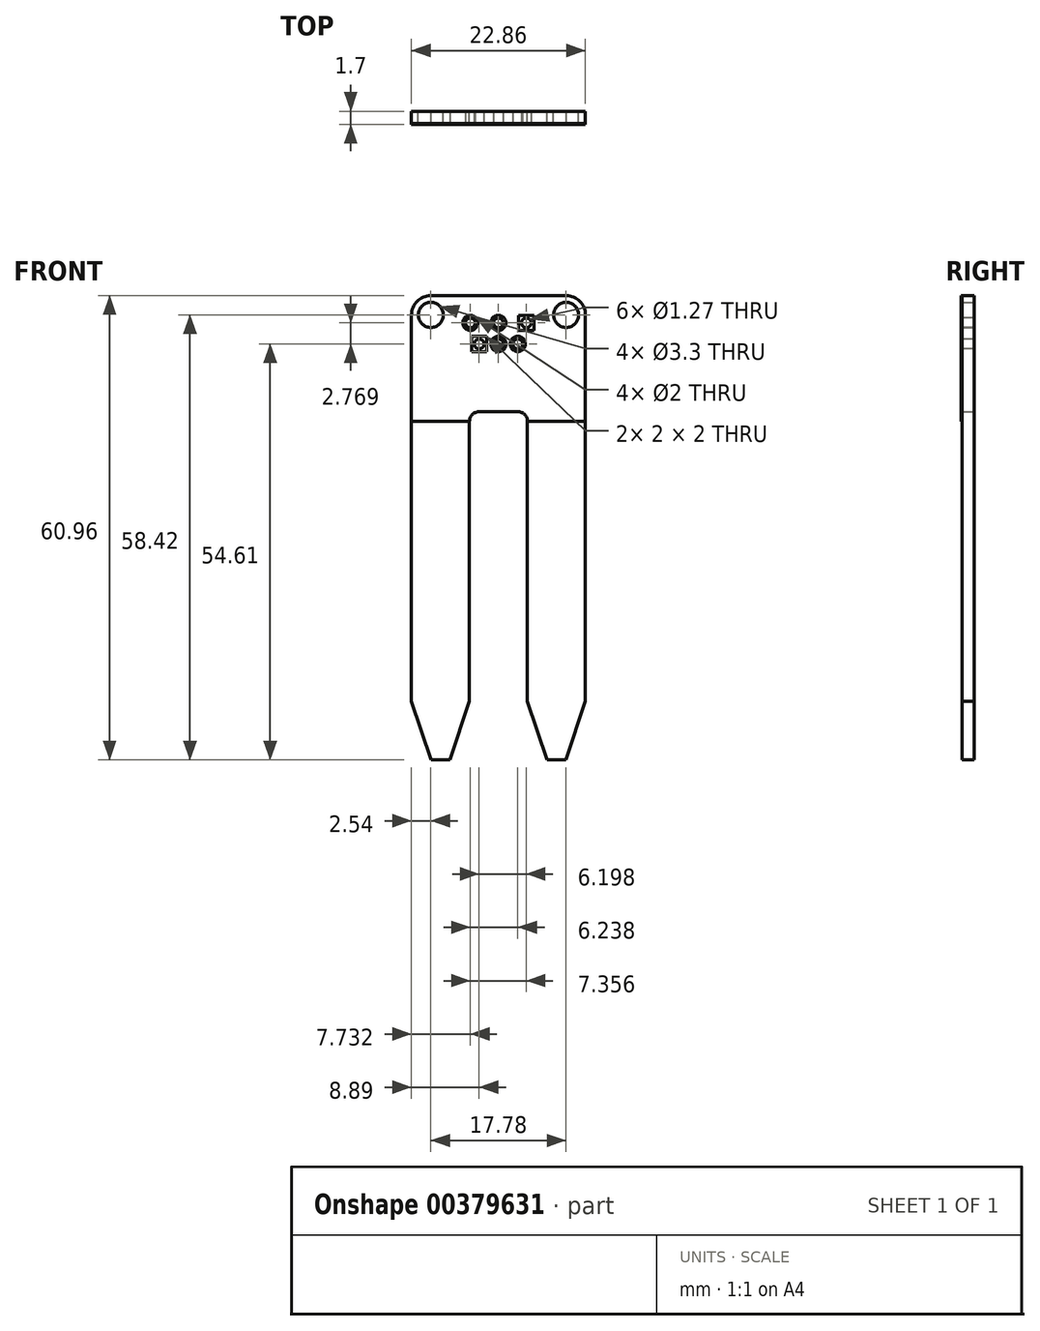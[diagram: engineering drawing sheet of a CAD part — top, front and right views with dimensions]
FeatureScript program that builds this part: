
annotation { "Feature Type Name" : "Feature", "Feature Type Description" : "" }
export const myFeature = defineFeature(function(context is Context, id is Id, definition is map)
    precondition{}
    {
        {
            var Q0;
            Q0=qCreatedBy(makeId("Front.planeOp"),FACE);
            var sketch = newSketch(context, id + "F0", { "sketchPlane" : qUnion([Q0])});
            skLineSegment(sketch, "E0.bottom", {"start": v(0, 0) * mm, "end": v(22.86, 0) * mm});
            skLineSegment(sketch, "E0.top", {"start": v(0, -15.24) * mm, "end": v(22.86, -15.24) * mm});
            skLineSegment(sketch, "E0.left", {"start": v(0, 0) * mm, "end": v(0, -15.24) * mm});
            skLineSegment(sketch, "E0.right", {"start": v(22.86, 0) * mm, "end": v(22.86, -15.24) * mm});
            skLineSegment(sketch, "E1.bottom", {"start": v(0, -15.24) * mm, "end": v(7.62, -15.24) * mm});
            skLineSegment(sketch, "E1.top", {"start": v(0, -60.96) * mm, "end": v(7.62, -60.96) * mm});
            skLineSegment(sketch, "E1.left", {"start": v(0, -15.24) * mm, "end": v(0, -60.96) * mm});
            skLineSegment(sketch, "E1.right", {"start": v(7.62, -15.24) * mm, "end": v(7.62, -60.96) * mm});
            skLineSegment(sketch, "E2.bottom", {"start": v(22.86, -15.24) * mm, "end": v(15.24, -15.24) * mm});
            skLineSegment(sketch, "E2.top", {"start": v(22.86, -60.96) * mm, "end": v(15.24, -60.96) * mm});
            skLineSegment(sketch, "E2.left", {"start": v(22.86, -15.24) * mm, "end": v(22.86, -60.96) * mm});
            skLineSegment(sketch, "E2.right", {"start": v(15.24, -15.24) * mm, "end": v(15.24, -60.96) * mm});
            skCircle(sketch, "E3", {"center": v(2.54, -2.54) * mm, "radius": 1.65 * mm});
            skCircle(sketch, "E4", {"center": v(20.32, -2.54) * mm, "radius": 1.65 * mm});
            skSolve(sketch);
        }
        {
            var Q0;
            Q0=qSketchRegion(id+"F0",true);
            extrude(context, id + "F1", {"entities" : qUnion([Q0]), "depth" : 1.6 * mm});
        }
        {
            var Q0;
            Q0=makeQuery(id+"F1.opExtrude","SWEPT_EDGE",EDGE,{"disambiguationData":[OSD([sQuery(id+"F0.wireOp",EDGE,"E0.bottom"),sQuery(id+"F0.wireOp",EDGE,"E0.left")])]});
            var Q1;
            Q1=makeQuery(id+"F1.opExtrude","SWEPT_EDGE",EDGE,{"disambiguationData":[OSD([sQuery(id+"F0.wireOp",EDGE,"E0.bottom"),sQuery(id+"F0.wireOp",EDGE,"E0.right")])]});
            fillet(context, id + "F2", {"entities" : qUnion([Q0, Q1]), "radius" : 2.54 * mm, "tangentPropagation" : true, "allowEdgeOverflow" : false});
        }
        {
            var Q0;
            Q0=makeQuery(id+"F1.opExtrude","SWEPT_EDGE",EDGE,{"disambiguationData":[OSD([sQuery(id+"F0.wireOp",EDGE,"E1.top"),sQuery(id+"F0.wireOp",EDGE,"E1.left")])]});
            var Q1;
            Q1=makeQuery(id+"F1.opExtrude","SWEPT_EDGE",EDGE,{"disambiguationData":[OSD([sQuery(id+"F0.wireOp",EDGE,"E1.top"),sQuery(id+"F0.wireOp",EDGE,"E1.right")])]});
            var Q2;
            Q2=makeQuery(id+"F1.opExtrude","SWEPT_EDGE",EDGE,{"disambiguationData":[OSD([sQuery(id+"F0.wireOp",EDGE,"E2.top"),sQuery(id+"F0.wireOp",EDGE,"E2.right")])]});
            chamfer(context, id + "F3", {"entities" : qUnion([Q0, Q1, Q2]), "chamferType" : ChamferType.TWO_OFFSETS, "width1" : 2.59 * mm, "oppositeDirection" : false, "width2" : 7.66 * mm, "tangentPropagation" : true});
        }
        {
            var Q0;
            Q0=makeQuery(id+"F1.opExtrude","SWEPT_EDGE",EDGE,{"disambiguationData":[OSD([sQuery(id+"F0.wireOp",EDGE,"E2.top"),sQuery(id+"F0.wireOp",EDGE,"E2.left")])]});
            chamfer(context, id + "F4", {"entities" : qUnion([Q0]), "chamferType" : ChamferType.TWO_OFFSETS, "width1" : 7.66 * mm, "oppositeDirection" : false, "width2" : 2.59 * mm, "tangentPropagation" : true});
        }
        {
            var Q0;
            Q0=makeQuery(id+"F1.opExtrude","SWEPT_EDGE",EDGE,{"disambiguationData":[OSD([sQuery(id+"F0.wireOp",EDGE,"E0.top"),sQuery(id+"F0.wireOp",EDGE,"E1.bottom"),sQuery(id+"F0.wireOp",EDGE,"E1.right")])]});
            var Q1;
            Q1=makeQuery(id+"F1.opExtrude","SWEPT_EDGE",EDGE,{"disambiguationData":[OSD([sQuery(id+"F0.wireOp",EDGE,"E0.top"),sQuery(id+"F0.wireOp",EDGE,"E2.bottom"),sQuery(id+"F0.wireOp",EDGE,"E2.right")])]});
            fillet(context, id + "F5", {"entities" : qUnion([Q0, Q1]), "radius" : 1.27 * mm, "tangentPropagation" : true, "allowEdgeOverflow" : false});
        }
        {
            var Q0;
            Q0=makeQuery(id+"F1.opExtrude","CAP_FACE",FACE,{"disambiguationData":[OSD([sQuery(id+"F0.wireOp",EDGE,"E0.bottom"),sQuery(id+"F0.wireOp",EDGE,"E0.top"),sQuery(id+"F0.wireOp",EDGE,"E0.left"),sQuery(id+"F0.wireOp",EDGE,"E0.right"),sQuery(id+"F0.wireOp",EDGE,"E1.top"),sQuery(id+"F0.wireOp",EDGE,"E1.left"),sQuery(id+"F0.wireOp",EDGE,"E1.right"),sQuery(id+"F0.wireOp",EDGE,"E2.top"),sQuery(id+"F0.wireOp",EDGE,"E2.left"),sQuery(id+"F0.wireOp",EDGE,"E2.right"),sQuery(id+"F0.wireOp",EDGE,"E3"),sQuery(id+"F0.wireOp",EDGE,"E4")])],"isStart":false});
            var sketch = newSketch(context, id + "F6", { "sketchPlane" : qUnion([Q0])});
            skCircle(sketch, "E5", {"center": v(7.73, -3.58) * mm, "radius": 0.64 * mm});
            skCircle(sketch, "E6.1.0.0", {"center": v(11.4, -3.58) * mm, "radius": 0.64 * mm});
            skCircle(sketch, "E6.2.0.0", {"center": v(15.09, -3.58) * mm, "radius": 0.64 * mm});
            skLineSegment(sketch, "E6.direction1", {"start": v(7.73, -3.58) * mm, "end": v(11.4, -3.58) * mm, "construction": true});
            skCircle(sketch, "E7", {"center": v(8.9, -6.35) * mm, "radius": 0.64 * mm});
            skCircle(sketch, "E8.1.0.0", {"center": v(11.43, -6.35) * mm, "radius": 0.64 * mm});
            skCircle(sketch, "E8.2.0.0", {"center": v(13.97, -6.35) * mm, "radius": 0.64 * mm});
            skLineSegment(sketch, "E8.direction1", {"start": v(8.9, -6.35) * mm, "end": v(11.43, -6.35) * mm, "construction": true});
            skSolve(sketch);
        }
        {
            var Q0;
            Q0=qSketchRegion(id+"F6",true);
            extrude(context, id + "F7", {"entities" : qUnion([Q0]), "operationType" : NewBodyOperationType.REMOVE, "endBound" : BoundingType.THROUGH_ALL, "oppositeDirection" : true, "depth" : 25 * mm});
        }
        {
            var Q0;
            Q0=makeQuery(id+"F1.opExtrude","CAP_FACE",FACE,{"disambiguationData":[OSD([sQuery(id+"F0.wireOp",EDGE,"E0.bottom"),sQuery(id+"F0.wireOp",EDGE,"E0.top"),sQuery(id+"F0.wireOp",EDGE,"E0.left"),sQuery(id+"F0.wireOp",EDGE,"E0.right"),sQuery(id+"F0.wireOp",EDGE,"E1.top"),sQuery(id+"F0.wireOp",EDGE,"E1.left"),sQuery(id+"F0.wireOp",EDGE,"E1.right"),sQuery(id+"F0.wireOp",EDGE,"E2.top"),sQuery(id+"F0.wireOp",EDGE,"E2.left"),sQuery(id+"F0.wireOp",EDGE,"E2.right"),sQuery(id+"F0.wireOp",EDGE,"E3"),sQuery(id+"F0.wireOp",EDGE,"E4")])],"isStart":false});
            var sketch = newSketch(context, id + "F8", { "sketchPlane" : qUnion([Q0])});
            skCircle(sketch, "E9", {"center": v(2.54, -2.54) * mm, "radius": 1.65 * mm});
            skCircle(sketch, "E10", {"center": v(20.32, -2.54) * mm, "radius": 1.65 * mm});
            skCircle(sketch, "E11", {"center": v(7.73, -3.58) * mm, "radius": 1 * mm});
            skCircle(sketch, "E12", {"center": v(11.4, -3.58) * mm, "radius": 1 * mm});
            skCircle(sketch, "E13", {"center": v(11.43, -6.35) * mm, "radius": 1 * mm});
            skCircle(sketch, "E14", {"center": v(13.97, -6.35) * mm, "radius": 1 * mm});
            skLineSegment(sketch, "E15", {"start": v(0, -16.5) * mm, "end": v(22.86, -16.5) * mm});
            skLineSegment(sketch, "E16", {"start": v(22.86, -16.5) * mm, "end": v(22.86, -2.54) * mm});
            skLineSegment(sketch, "E17", {"start": v(20.32, 0) * mm, "end": v(2.54, 0) * mm});
            skLineSegment(sketch, "E18", {"start": v(0, -2.54) * mm, "end": v(0, -16.5) * mm});
            skPoint(sketch, "E19.visualSharp", {"position": v(0, 0) * mm});
            skArc(sketch, "E19.filletArc", {"start": v(2.54, 0) * mm, "mid": v(0.74, -0.74) * mm, "end": v(0, -2.54) * mm});
            skPoint(sketch, "E20.visualSharp", {"position": v(22.86, 0) * mm});
            skArc(sketch, "E20.filletArc", {"start": v(22.86, -2.54) * mm, "mid": v(22.12, -0.74) * mm, "end": v(20.32, 0) * mm});
            skLineSegment(sketch, "E21", {"start": v(7.62, -16.5) * mm, "end": v(7.62, -16.5) * mm});
            skLineSegment(sketch, "E22", {"start": v(8.9, -15.24) * mm, "end": v(13.97, -15.24) * mm});
            skLineSegment(sketch, "E23", {"start": v(15.24, -16.5) * mm, "end": v(15.24, -16.5) * mm});
            skPoint(sketch, "E24.visualSharp", {"position": v(7.62, -15.24) * mm});
            skArc(sketch, "E24.filletArc", {"start": v(8.9, -15.24) * mm, "mid": v(8, -15.61) * mm, "end": v(7.62, -16.5) * mm});
            skPoint(sketch, "E25.visualSharp", {"position": v(15.24, -15.24) * mm});
            skArc(sketch, "E25.filletArc", {"start": v(15.24, -16.5) * mm, "mid": v(14.87, -15.61) * mm, "end": v(13.97, -15.24) * mm});
            skLineSegment(sketch, "E26.bottom", {"start": v(16.09, -2.58) * mm, "end": v(14.09, -2.58) * mm});
            skLineSegment(sketch, "E26.top", {"start": v(16.09, -4.58) * mm, "end": v(14.09, -4.58) * mm});
            skLineSegment(sketch, "E26.left", {"start": v(16.09, -2.58) * mm, "end": v(16.09, -4.58) * mm});
            skLineSegment(sketch, "E26.right", {"start": v(14.09, -2.58) * mm, "end": v(14.09, -4.58) * mm});
            skPoint(sketch, "E26.middle", {"position": v(15.09, -3.58) * mm});
            skLineSegment(sketch, "E27.bottom", {"start": v(7.9, -7.35) * mm, "end": v(9.9, -7.35) * mm});
            skLineSegment(sketch, "E27.top", {"start": v(7.9, -5.35) * mm, "end": v(9.9, -5.35) * mm});
            skLineSegment(sketch, "E27.left", {"start": v(7.9, -7.35) * mm, "end": v(7.9, -5.35) * mm});
            skLineSegment(sketch, "E27.right", {"start": v(9.9, -7.35) * mm, "end": v(9.9, -5.35) * mm});
            skPoint(sketch, "E27.middle", {"position": v(8.9, -6.35) * mm});
            skSolve(sketch);
        }
        {
            var Q0;
            Q0=makeQuery(id+"F8.imprint","IMPRINT",FACE,{"disambiguationData":[TD([[makeQuery(id+"F8.imprint","IMPRINT",EDGE,{"derivedFrom":sQuery(id+"F8.wireOp",EDGE,"E9")}),-1.0]])]});
            extrude(context, id + "F9", {"entities" : qUnion([Q0]), "depth" : .1 * mm});
        }
    });
